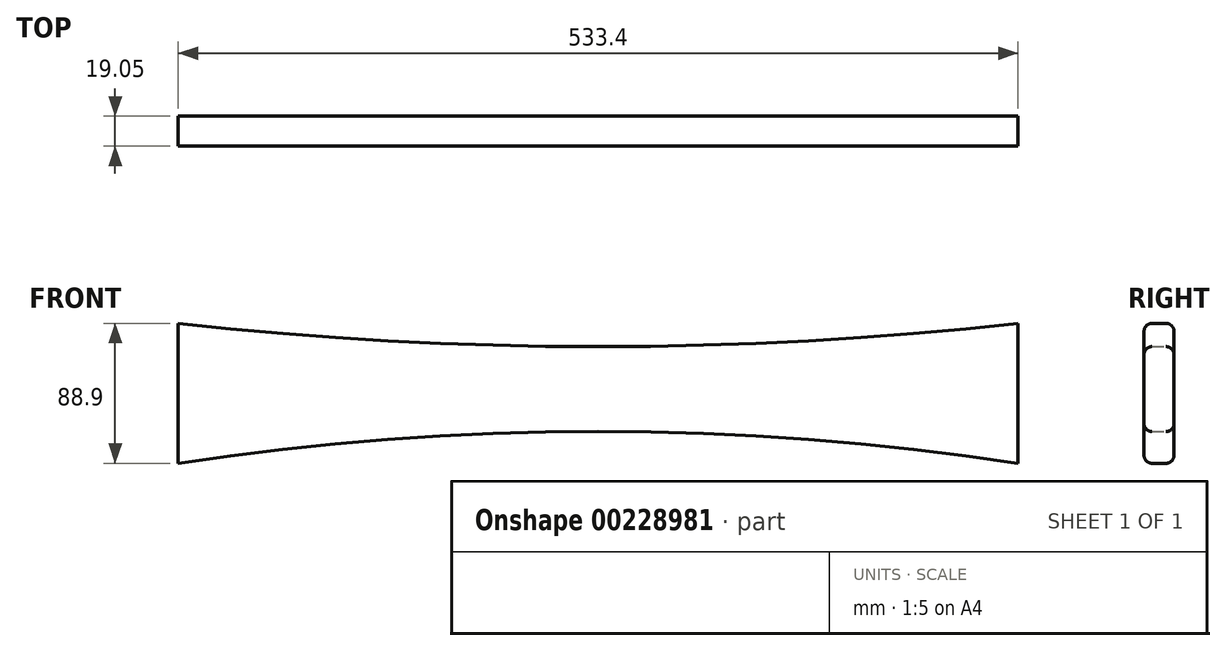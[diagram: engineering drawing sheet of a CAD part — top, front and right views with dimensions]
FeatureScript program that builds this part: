
annotation { "Feature Type Name" : "Feature", "Feature Type Description" : "" }
export const myFeature = defineFeature(function(context is Context, id is Id, definition is map)
    precondition{}
    {
        {
            var Q0;
            Q0=qCreatedBy(makeId("Front.planeOp"),FACE);
            var sketch = newSketch(context, id + "F0", { "sketchPlane" : qUnion([Q0])});
            skLineSegment(sketch, "E0.left", {"start": v(-266.7, 44.45) * mm, "end": v(-266.7, -44.45) * mm});
            skLineSegment(sketch, "E0.right", {"start": v(266.7, 44.45) * mm, "end": v(266.7, -44.45) * mm});
            skPoint(sketch, "E0.middle", {"position": v(0, 0) * mm});
            skArc(sketch, "E1", {"start": v(266.7, -44.45) * mm, "mid": v(0, -24.33) * mm, "end": v(-266.7, -44.45) * mm});
            skArc(sketch, "E2", {"start": v(-266.7, 44.45) * mm, "mid": v(0, 29.67) * mm, "end": v(266.7, 44.45) * mm});
            skSolve(sketch);
        }
        {
            var Q0;
            Q0 = qSketchRegion(id + "F0", true);
            extrude(context, id + "F1", {"entities" : qUnion([Q0]), "depth" : 19.05 * mm});
        }
        {
            var Q0;
            Q0=makeQuery(id+"F1.opExtrude","CAP_EDGE",EDGE,{"disambiguationData":[OSD([sQuery(id+"F0.wireOp",EDGE,"E2")])],"isStart":false});
            var Q1;
            Q1=makeQuery(id+"F1.opExtrude","CAP_EDGE",EDGE,{"disambiguationData":[OSD([sQuery(id+"F0.wireOp",EDGE,"E1")])],"isStart":false});
            var Q2;
            Q2=makeQuery(id+"F1.opExtrude","CAP_EDGE",EDGE,{"disambiguationData":[OSD([sQuery(id+"F0.wireOp",EDGE,"E2")])],"isStart":true});
            var Q3;
            Q3=makeQuery(id+"F1.opExtrude","CAP_EDGE",EDGE,{"disambiguationData":[OSD([sQuery(id+"F0.wireOp",EDGE,"E1")])],"isStart":true});
            fillet(context, id + "F2", {"entities" : qUnion([Q0, Q1, Q2, Q3]), "radius" : 5.08 * mm, "tangentPropagation" : true, "allowEdgeOverflow" : false});
        }
    });
